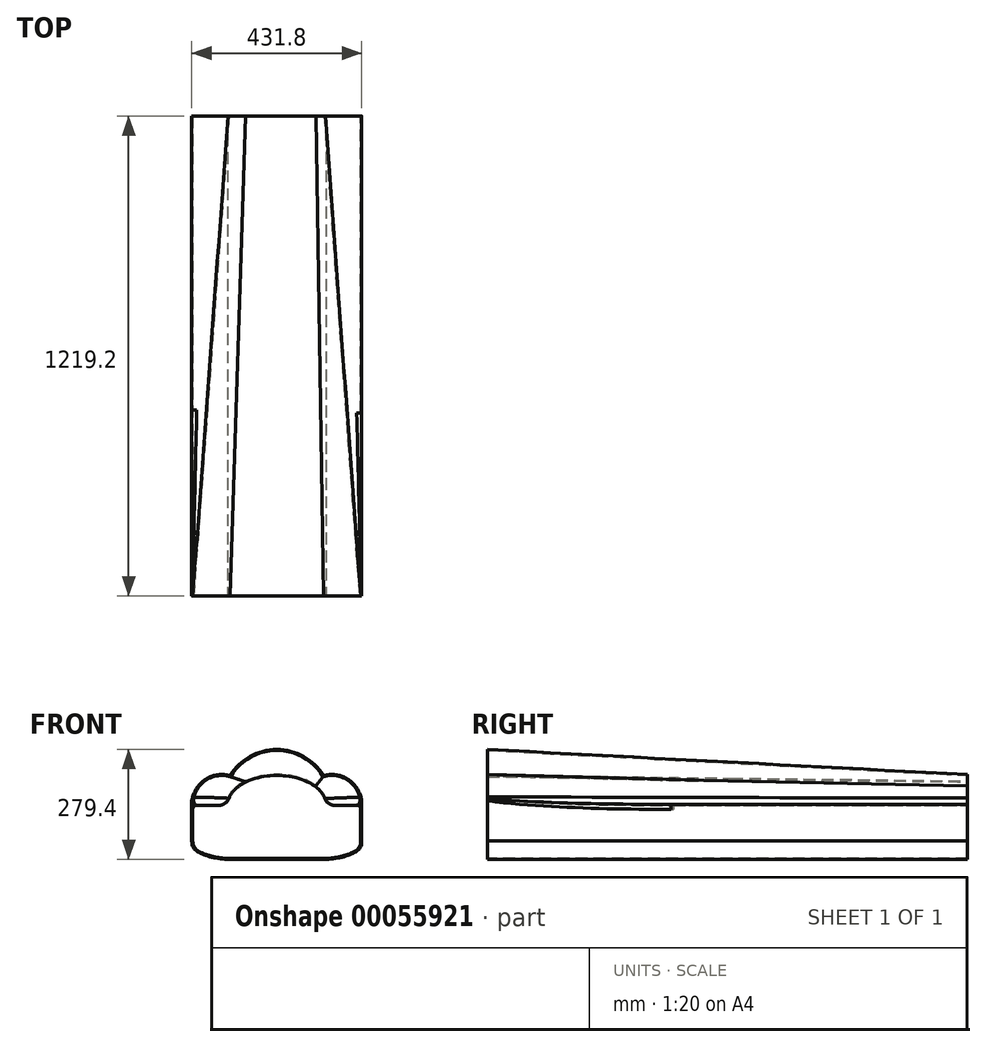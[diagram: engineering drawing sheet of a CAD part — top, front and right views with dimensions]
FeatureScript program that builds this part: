
annotation { "Feature Type Name" : "Feature", "Feature Type Description" : "" }
export const myFeature = defineFeature(function(context is Context, id is Id, definition is map)
    precondition{}
    {
        {
            var Q0;
            Q0=qCreatedBy(makeId("Front.planeOp"),FACE);
            var sketch = newSketch(context, id + "F0", { "sketchPlane" : qUnion([Q0])});
            skArc(sketch, "E0", {"start": v(118.92, 73.31) * mm, "mid": v(0, 139.7) * mm, "end": v(-118.92, 73.31) * mm});
            skArc(sketch, "E1", {"start": v(-118.92, 73.31) * mm, "mid": v(-215.9, 0) * mm, "end": v(-118.92, -73.31) * mm});
            skArc(sketch, "E2", {"start": v(118.92, -73.31) * mm, "mid": v(215.9, 0) * mm, "end": v(118.92, 73.31) * mm});
            skArc(sketch, "E3.trimOffspring", {"start": v(-118.92, -73.31) * mm, "mid": v(0, -139.7) * mm, "end": v(118.92, -73.31) * mm});
            skSolve(sketch);
        }
        {
            var Q0;
            Q0=qCreatedBy(makeId("Front.planeOp"),FACE);
            cPlane(context, id + "F1", {"entities" : qUnion([Q0]), "cplaneType" : CPlaneType.OFFSET, "offset" : 1219.2 * mm, "oppositeDirection" : true, "width" : 152.4 * mm, "height" : 152.4 * mm});
        }
        {
            var Q0;
            Q0=qCreatedBy(id+"F1.planeOp",FACE);
            var sketch = newSketch(context, id + "F2", { "sketchPlane" : qUnion([Q0])});
            skEllipse(sketch, "E4", {"center": v(0, 0) * mm, "majorRadius": 127 * mm, "minorRadius": 76.2 * mm, "majorAxis": v(-1, 0)});
            skSolve(sketch);
        }
        {
            var Q0;
            Q0=makeQuery(id+"F0.imprint","IMPRINT",FACE,{"disambiguationData":[TD([[makeQuery(id+"F0.imprint","IMPRINT",EDGE,{"derivedFrom":sQuery(id+"F0.wireOp",EDGE,"E0")}),1.0]])]});
            var Q1;
            Q1=makeQuery(id+"F2.imprint","IMPRINT",FACE,{"disambiguationData":[TD([[makeQuery(id+"F2.imprint","IMPRINT",EDGE,{"derivedFrom":sQuery(id+"F2.wireOp",EDGE,"E4")}),1.0]])]});
            loft(context, id + "F3", {"sheetProfilesArray" : [{ "sheetProfileEntities" : qUnion([Q0]) }, { "sheetProfileEntities" : qUnion([Q1]) }]});
        }
        {
            var Q0;
            Q0=makeQuery(id+"F3.opLoft","CAP_FACE",FACE,{"disambiguationData":[OSD([makeQuery(id+"F0.imprint","IMPRINT",FACE,{"disambiguationData":[TD([[makeQuery(id+"F0.imprint","IMPRINT",EDGE,{"derivedFrom":sQuery(id+"F0.wireOp",EDGE,"E0")}),1.0]])]})])],"isStart":true});
            var sketch = newSketch(context, id + "F4", { "sketchPlane" : qUnion([Q0])});
            skLineSegment(sketch, "E5", {"start": v(0, 0) * mm, "end": v(-215.9, 0) * mm});
            skLineSegment(sketch, "E6", {"start": v(0, -139.7) * mm, "end": v(-124.72, -139.7) * mm});
            skLineSegment(sketch, "E7", {"start": v(-215.9, 0) * mm, "end": v(-215.9, -92.78) * mm});
            skFitSpline(sketch, "E8", {"points": [v(-215.9, -92.78) * mm, v(-195.5, -123.25) * mm, v(-124.72, -139.7) * mm], "startDerivative": vector(1.48, -121) * mm, "endDerivative": vector(140.86, -5.25) * mm});
            skLineSegment(sketch, "E9", {"start": v(0, 0) * mm, "end": v(0, -53.72) * mm});
            skLineSegment(sketch, "E10.MirrorCS", {"start": v(0, 0) * mm, "end": v(215.9, 0) * mm});
            skLineSegment(sketch, "E11.MirrorCS", {"start": v(215.9, 0) * mm, "end": v(215.9, -92.78) * mm});
            skFitSpline(sketch, "E12.MirrorCS", {"points": [v(215.9, -92.78) * mm, v(195.5, -123.25) * mm, v(124.72, -139.7) * mm], "startDerivative": vector(-1.48, -121) * mm, "endDerivative": vector(-140.86, -5.25) * mm});
            skLineSegment(sketch, "E13.MirrorCS", {"start": v(0, -139.7) * mm, "end": v(124.72, -139.7) * mm});
            skSolve(sketch);
        }
        {
            var Q0;
            {var subQ6=sQuery(id+"F4.wireOp",EDGE,"E6");Q0=makeQuery(id+"F4.imprint","IMPRINT",FACE,{"disambiguationData":[TD([[makeQuery(id+"F4.imprint","IMPRINT",EDGE,{"derivedFrom":subQ6}),-1.0]])]});}
            var Q1;
            {var subQ5=sQuery(id+"F4.wireOp",EDGE,"E11.MirrorCS");Q1=makeQuery(id+"F4.imprint","IMPRINT",FACE,{"disambiguationData":[TD([[makeQuery(id+"F4.imprint","IMPRINT",EDGE,{"derivedFrom":subQ5}),-1.0]])]});}
            var Q2;
            {var subQ7=sQuery(id+"F4.wireOp",EDGE,"E5");Q2=makeQuery(id+"F4.imprint","IMPRINT",FACE,{"disambiguationData":[TD([[makeQuery(id+"F4.imprint","IMPRINT",EDGE,{"derivedFrom":subQ7}),1.0]])]});}
            extrude(context, id + "F5", {"entities" : qUnion([Q0, Q1, Q2]), "operationType" : NewBodyOperationType.ADD, "oppositeDirection" : true, "depth" : 1219.2 * mm});
        }
        {
            var Q0;
            {var subQ0=sQuery(id+"F2.wireOp",EDGE,"E4");var subQ1=sQuery(id+"F0.wireOp",EDGE,"E1");var subQ2=sQuery(id+"F0.wireOp",EDGE,"E3.trimOffspring");var subQ3=sQuery(id+"F0.wireOp",EDGE,"E2");var subQ4=sQuery(id+"F0.wireOp",EDGE,"E0");Q0=makeQuery(id+"F5.boolean.opBoolean","INTERSECT",EDGE,{"derivedFrom":[makeQuery(id+"F3.opLoft","SWEPT_FACE",FACE,{"disambiguationData":[OSD([subQ4,subQ1,subQ3,subQ2,subQ0]),TDD([makeQuery(id+"F0.imprint","INTERSECT",VERTEX,{"derivedFrom":[subQ4,subQ1]}),makeQuery(id+"F0.imprint","INTERSECT",VERTEX,{"derivedFrom":[subQ1,subQ2]}),makeQuery(id+"F0.imprint","INTERSECT",VERTEX,{"derivedFrom":[subQ3,subQ2]}),makeQuery(id+"F0.imprint","IMPRINT",EDGE,{"derivedFrom":subQ1}),makeQuery(id+"F2.imprint","IMPRINT",EDGE,{"derivedFrom":subQ0})])]}),makeQuery(id+"F5.opExtrude","SWEPT_FACE",FACE,{"disambiguationData":[OSD([sQuery(id+"F4.wireOp",EDGE,"E5"),sQuery(id+"F4.wireOp",EDGE,"E10.MirrorCS")])]})]});}
            var Q1;
            Q1=makeQuery(id+"F5.boolean.opBoolean","INTERSECT",EDGE,{"derivedFrom":[makeQuery(id+"F3.opLoft","SWEPT_FACE",FACE,{"disambiguationData":[OSD([sQuery(id+"F0.wireOp",EDGE,"E0"),sQuery(id+"F0.wireOp",EDGE,"E2"),sQuery(id+"F0.wireOp",EDGE,"E3.trimOffspring"),sQuery(id+"F2.wireOp",EDGE,"E4")])]}),makeQuery(id+"F5.opExtrude","SWEPT_FACE",FACE,{"disambiguationData":[OSD([sQuery(id+"F4.wireOp",EDGE,"E5"),sQuery(id+"F4.wireOp",EDGE,"E10.MirrorCS")])]})]});
            fillet(context, id + "F6", {"entities" : qUnion([Q0, Q1]), "radius" : 25.4 * mm, "tangentPropagation" : true, "allowEdgeOverflow" : false});
        }
        {
            var Q0;
            Q0=makeQuery(id+"F5.opExtrude","SWEPT_EDGE",EDGE,{"disambiguationData":[OSD([sQuery(id+"F0.wireOp",EDGE,"E0"),sQuery(id+"F0.wireOp",EDGE,"E1"),sQuery(id+"F0.wireOp",EDGE,"E3.trimOffspring"),sQuery(id+"F4.wireOp",EDGE,"E5"),sQuery(id+"F4.wireOp",EDGE,"E7")])]});
            var Q1;
            Q1=makeQuery(id+"F5.opExtrude","SWEPT_EDGE",EDGE,{"disambiguationData":[OSD([sQuery(id+"F0.wireOp",EDGE,"E0"),sQuery(id+"F0.wireOp",EDGE,"E2"),sQuery(id+"F0.wireOp",EDGE,"E3.trimOffspring"),sQuery(id+"F4.wireOp",EDGE,"E10.MirrorCS"),sQuery(id+"F4.wireOp",EDGE,"E11.MirrorCS")])]});
            fillet(context, id + "F7", {"entities" : qUnion([Q0, Q1]), "radius" : 12.7 * mm, "tangentPropagation" : true, "allowEdgeOverflow" : false});
        }
        {
            var Q0;
            Q0=makeQuery(id+"F5.boolean.opBoolean","MERGE",FACE,{"derivedFrom":[makeQuery(id+"F3.opLoft","CAP_FACE",FACE,{"disambiguationData":[OSD([makeQuery(id+"F0.imprint","IMPRINT",FACE,{"disambiguationData":[TD([[makeQuery(id+"F0.imprint","IMPRINT",EDGE,{"derivedFrom":sQuery(id+"F0.wireOp",EDGE,"E0")}),1.0]])]})])],"isStart":true}),makeQuery(id+"F5.opExtrude","CAP_FACE",FACE,{"disambiguationData":[OSD([sQuery(id+"F4.wireOp",EDGE,"E5"),sQuery(id+"F4.wireOp",EDGE,"E6"),sQuery(id+"F4.wireOp",EDGE,"E7"),sQuery(id+"F4.wireOp",EDGE,"E8"),sQuery(id+"F4.wireOp",EDGE,"E10.MirrorCS"),sQuery(id+"F4.wireOp",EDGE,"E11.MirrorCS"),sQuery(id+"F4.wireOp",EDGE,"E12.MirrorCS"),sQuery(id+"F4.wireOp",EDGE,"E13.MirrorCS")])],"isStart":true})]});
            var Q1;
            Q1=makeQuery(id+"F5.boolean.opBoolean","MERGE",FACE,{"derivedFrom":[makeQuery(id+"F3.opLoft","CAP_FACE",FACE,{"disambiguationData":[OSD([makeQuery(id+"F2.imprint","IMPRINT",FACE,{"disambiguationData":[TD([[makeQuery(id+"F2.imprint","IMPRINT",EDGE,{"derivedFrom":sQuery(id+"F2.wireOp",EDGE,"E4")}),1.0]])]})])],"isStart":true}),makeQuery(id+"F5.opExtrude","CAP_FACE",FACE,{"disambiguationData":[OSD([sQuery(id+"F4.wireOp",EDGE,"E5"),sQuery(id+"F4.wireOp",EDGE,"E6"),sQuery(id+"F4.wireOp",EDGE,"E7"),sQuery(id+"F4.wireOp",EDGE,"E8"),sQuery(id+"F4.wireOp",EDGE,"E10.MirrorCS"),sQuery(id+"F4.wireOp",EDGE,"E11.MirrorCS"),sQuery(id+"F4.wireOp",EDGE,"E12.MirrorCS"),sQuery(id+"F4.wireOp",EDGE,"E13.MirrorCS")])],"isStart":false})]});
            shell(context, id + "F8", {"entities" : qUnion([Q0, Q1]), "thickness" : 2.54 * mm});
        }
    });
